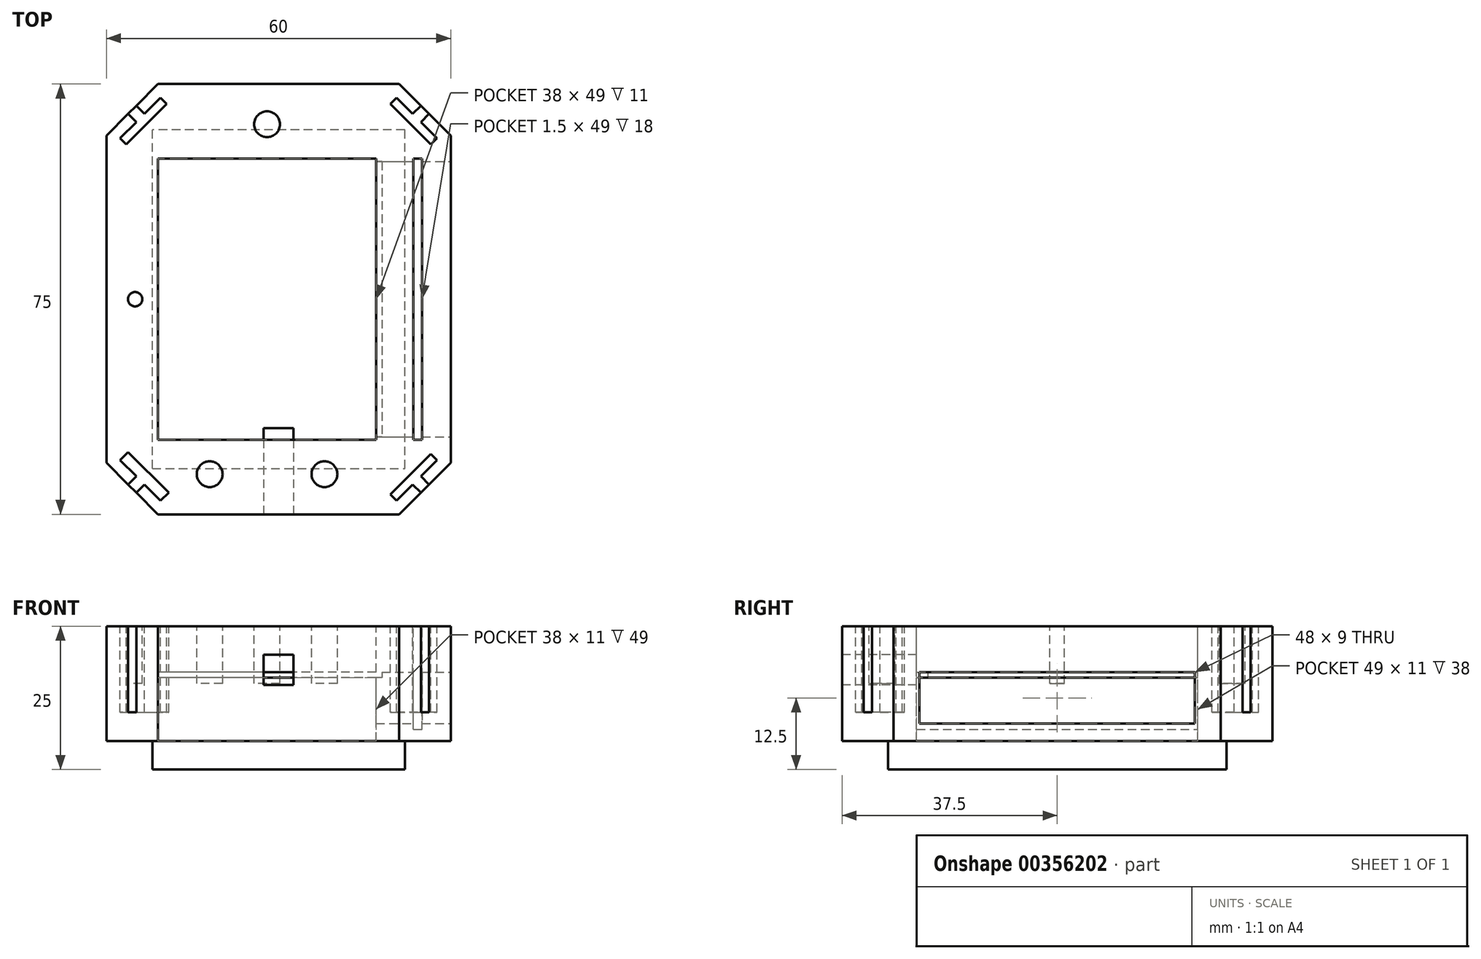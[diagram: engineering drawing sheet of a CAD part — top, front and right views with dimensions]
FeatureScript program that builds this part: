
annotation { "Feature Type Name" : "Feature", "Feature Type Description" : "" }
export const myFeature = defineFeature(function(context is Context, id is Id, definition is map)
    precondition{}
    {
        {
            var Q0;
            Q0=qCreatedBy(makeId("Top.planeOp"),FACE);
            var sketch = newSketch(context, id + "F0", { "sketchPlane" : qUnion([Q0])});
            skPoint(sketch, "E0", {"position": v(0, 66) * mm});
            skPoint(sketch, "E1", {"position": v(9, 75) * mm});
            skPoint(sketch, "E2", {"position": v(51, 75) * mm});
            skPoint(sketch, "E3", {"position": v(60, 66) * mm});
            skPoint(sketch, "E4", {"position": v(0, 9) * mm});
            skPoint(sketch, "E5", {"position": v(9, 0) * mm});
            skPoint(sketch, "E6", {"position": v(51, 0) * mm});
            skPoint(sketch, "E7", {"position": v(60, 9) * mm});
            skLineSegment(sketch, "E8", {"start": v(0, 9) * mm, "end": v(9, 0) * mm});
            skLineSegment(sketch, "E9", {"start": v(51, 0) * mm, "end": v(9, 0) * mm});
            skLineSegment(sketch, "E10", {"start": v(51, 0) * mm, "end": v(60, 9) * mm});
            skLineSegment(sketch, "E11", {"start": v(60, 9) * mm, "end": v(60, 66) * mm});
            skLineSegment(sketch, "E12", {"start": v(60, 66) * mm, "end": v(51, 75) * mm});
            skLineSegment(sketch, "E13", {"start": v(51, 75) * mm, "end": v(9, 75) * mm});
            skLineSegment(sketch, "E14", {"start": v(9, 75) * mm, "end": v(0, 66) * mm});
            skLineSegment(sketch, "E15", {"start": v(0, 66) * mm, "end": v(0, 9) * mm});
            skPoint(sketch, "E16", {"position": v(0, 63) * mm});
            skSolve(sketch);
        }
        {
            var Q0;
            Q0 = qSketchRegion(id + "F0", true);
            extrude(context, id + "F1", {"entities" : qUnion([Q0]), "depth" : 20 * mm, "offsetDistance" : 25 * mm});
        }
        {
            var Q0;
            Q0 = qSketchRegion(id + "F0", true);
            extrude(context, id + "F2", {"entities" : qUnion([Q0]), "operationType" : NewBodyOperationType.ADD, "depth" : 20 * mm, "offsetDistance" : 25 * mm});
        }
        {
            var Q0;
            Q0=makeQuery(id+"F1.opExtrude","CAP_FACE",FACE,{"disambiguationData":[OSD([sQuery(id+"F0.wireOp",EDGE,"E8"),sQuery(id+"F0.wireOp",EDGE,"E9"),sQuery(id+"F0.wireOp",EDGE,"E10"),sQuery(id+"F0.wireOp",EDGE,"E11"),sQuery(id+"F0.wireOp",EDGE,"E12"),sQuery(id+"F0.wireOp",EDGE,"E13"),sQuery(id+"F0.wireOp",EDGE,"E14"),sQuery(id+"F0.wireOp",EDGE,"E15")])],"isStart":false});
            var sketch = newSketch(context, id + "F3", { "sketchPlane" : qUnion([Q0])});
            skPoint(sketch, "E17", {"position": v(4.5, 70.5) * mm});
            skPoint(sketch, "E18", {"position": v(5.2, 71.2) * mm});
            skPoint(sketch, "E19", {"position": v(3.8, 69.8) * mm});
            skPoint(sketch, "E20", {"position": v(3.8, 5.2) * mm});
            skPoint(sketch, "E21", {"position": v(4.5, 4.5) * mm});
            skPoint(sketch, "E22", {"position": v(5.2, 3.8) * mm});
            skPoint(sketch, "E23", {"position": v(54.8, 3.8) * mm});
            skPoint(sketch, "E24", {"position": v(55.5, 4.5) * mm});
            skPoint(sketch, "E25", {"position": v(56.2, 5.2) * mm});
            skPoint(sketch, "E26", {"position": v(56.2, 69.8) * mm});
            skPoint(sketch, "E27", {"position": v(55.5, 70.5) * mm});
            skPoint(sketch, "E28", {"position": v(54.8, 71.2) * mm});
            skLineSegment(sketch, "E29", {"start": v(3.8, 69.8) * mm, "end": v(5.2, 71.2) * mm});
            skLineSegment(sketch, "E30", {"start": v(5.2, 71.2) * mm, "end": v(6.62, 69.8) * mm});
            skLineSegment(sketch, "E31", {"start": v(6.62, 69.8) * mm, "end": v(5.2, 68.38) * mm});
            skLineSegment(sketch, "E32", {"start": v(5.2, 68.38) * mm, "end": v(3.8, 69.8) * mm});
            skLineSegment(sketch, "E33", {"start": v(6.62, 69.8) * mm, "end": v(9.45, 72.62) * mm});
            skLineSegment(sketch, "E34", {"start": v(9.45, 72.62) * mm, "end": v(5.2, 68.38) * mm});
            skLineSegment(sketch, "E35", {"start": v(5.2, 68.38) * mm, "end": v(2.38, 65.55) * mm});
            skLineSegment(sketch, "E36", {"start": v(2.38, 65.55) * mm, "end": v(3.44, 64.49) * mm});
            skLineSegment(sketch, "E37", {"start": v(3.44, 64.49) * mm, "end": v(10.51, 71.56) * mm});
            skLineSegment(sketch, "E38", {"start": v(10.51, 71.56) * mm, "end": v(9.45, 72.62) * mm});
            skLineSegment(sketch, "E39", {"start": v(54.8, 71.2) * mm, "end": v(56.2, 69.8) * mm});
            skLineSegment(sketch, "E40", {"start": v(56.2, 69.8) * mm, "end": v(54.8, 68.38) * mm});
            skLineSegment(sketch, "E41", {"start": v(54.8, 68.38) * mm, "end": v(53.38, 69.8) * mm});
            skLineSegment(sketch, "E42", {"start": v(53.38, 69.8) * mm, "end": v(54.8, 71.2) * mm});
            skLineSegment(sketch, "E43", {"start": v(53.38, 69.8) * mm, "end": v(50.55, 72.62) * mm});
            skLineSegment(sketch, "E44", {"start": v(50.55, 72.62) * mm, "end": v(49.49, 71.56) * mm});
            skLineSegment(sketch, "E45", {"start": v(49.49, 71.56) * mm, "end": v(56.56, 64.49) * mm});
            skLineSegment(sketch, "E46", {"start": v(56.56, 64.49) * mm, "end": v(57.62, 65.55) * mm});
            skLineSegment(sketch, "E47", {"start": v(57.62, 65.55) * mm, "end": v(54.8, 68.38) * mm});
            skLineSegment(sketch, "E48", {"start": v(54.8, 3.8) * mm, "end": v(56.2, 5.2) * mm});
            skLineSegment(sketch, "E49", {"start": v(56.2, 5.2) * mm, "end": v(54.8, 6.62) * mm});
            skLineSegment(sketch, "E50", {"start": v(54.8, 6.62) * mm, "end": v(53.38, 5.2) * mm});
            skLineSegment(sketch, "E51", {"start": v(53.38, 5.2) * mm, "end": v(54.8, 3.8) * mm});
            skLineSegment(sketch, "E52", {"start": v(54.8, 6.62) * mm, "end": v(57.62, 9.45) * mm});
            skLineSegment(sketch, "E53", {"start": v(57.62, 9.45) * mm, "end": v(56.56, 10.51) * mm});
            skLineSegment(sketch, "E54", {"start": v(56.56, 10.51) * mm, "end": v(49.49, 3.44) * mm});
            skLineSegment(sketch, "E55", {"start": v(49.49, 3.44) * mm, "end": v(50.55, 2.38) * mm});
            skLineSegment(sketch, "E56", {"start": v(50.55, 2.38) * mm, "end": v(53.38, 5.2) * mm});
            skLineSegment(sketch, "E57", {"start": v(3.8, 5.2) * mm, "end": v(5.2, 3.8) * mm});
            skLineSegment(sketch, "E58", {"start": v(5.2, 3.8) * mm, "end": v(6.62, 5.2) * mm});
            skLineSegment(sketch, "E59", {"start": v(6.62, 5.2) * mm, "end": v(5.2, 6.62) * mm});
            skLineSegment(sketch, "E60", {"start": v(5.2, 6.62) * mm, "end": v(3.8, 5.2) * mm});
            skLineSegment(sketch, "E61", {"start": v(5.2, 6.62) * mm, "end": v(2.38, 9.45) * mm});
            skLineSegment(sketch, "E62", {"start": v(2.38, 9.45) * mm, "end": v(3.8, 10.86) * mm});
            skLineSegment(sketch, "E63", {"start": v(3.8, 10.86) * mm, "end": v(10.86, 3.8) * mm});
            skLineSegment(sketch, "E64", {"start": v(10.86, 3.8) * mm, "end": v(9.45, 2.38) * mm});
            skLineSegment(sketch, "E65", {"start": v(9.45, 2.38) * mm, "end": v(6.62, 5.2) * mm});
            skSolve(sketch);
        }
        {
            var Q0;
            Q0=makeQuery(id+"F3.imprint","IMPRINT",FACE,{"disambiguationData":[TD([[makeQuery(id+"F3.imprint","IMPRINT",EDGE,{"derivedFrom":sQuery(id+"F3.wireOp",EDGE,"E29")}),1.0]])]});
            var Q1;
            {var subQ0=sQuery(id+"F3.wireOp",EDGE,"E35");Q1=makeQuery(id+"F3.imprint","IMPRINT",FACE,{"disambiguationData":[TD([[makeQuery(id+"F3.imprint","IMPRINT",EDGE,{"derivedFrom":subQ0}),1.0]])]});}
            var Q2;
            Q2=makeQuery(id+"F3.imprint","IMPRINT",FACE,{"disambiguationData":[TD([[makeQuery(id+"F3.imprint","IMPRINT",EDGE,{"derivedFrom":sQuery(id+"F3.wireOp",EDGE,"E59")}),-1.0]])]});
            var Q3;
            Q3=makeQuery(id+"F3.imprint","IMPRINT",FACE,{"disambiguationData":[TD([[makeQuery(id+"F3.imprint","IMPRINT",EDGE,{"derivedFrom":sQuery(id+"F3.wireOp",EDGE,"E57")}),1.0]])]});
            var Q4;
            Q4=makeQuery(id+"F3.imprint","IMPRINT",FACE,{"disambiguationData":[TD([[makeQuery(id+"F3.imprint","IMPRINT",EDGE,{"derivedFrom":sQuery(id+"F3.wireOp",EDGE,"E48")}),1.0]])]});
            var Q5;
            Q5=makeQuery(id+"F3.imprint","IMPRINT",FACE,{"disambiguationData":[TD([[makeQuery(id+"F3.imprint","IMPRINT",EDGE,{"derivedFrom":sQuery(id+"F3.wireOp",EDGE,"E50")}),-1.0]])]});
            var Q6;
            Q6=makeQuery(id+"F3.imprint","IMPRINT",FACE,{"disambiguationData":[TD([[makeQuery(id+"F3.imprint","IMPRINT",EDGE,{"derivedFrom":sQuery(id+"F3.wireOp",EDGE,"E41")}),1.0]])]});
            var Q7;
            Q7=makeQuery(id+"F3.imprint","IMPRINT",FACE,{"disambiguationData":[TD([[makeQuery(id+"F3.imprint","IMPRINT",EDGE,{"derivedFrom":sQuery(id+"F3.wireOp",EDGE,"E39")}),1.0]])]});
            extrude(context, id + "F4", {"entities" : qUnion([Q0, Q1, Q2, Q3, Q4, Q5, Q6, Q7]), "operationType" : NewBodyOperationType.REMOVE, "oppositeDirection" : true, "depth" : 15 * mm, "offsetDistance" : 25 * mm});
        }
        {
            var Q0;
            Q0=makeQuery(id+"F1.opExtrude","CAP_FACE",FACE,{"disambiguationData":[OSD([sQuery(id+"F0.wireOp",EDGE,"E8"),sQuery(id+"F0.wireOp",EDGE,"E9"),sQuery(id+"F0.wireOp",EDGE,"E10"),sQuery(id+"F0.wireOp",EDGE,"E11"),sQuery(id+"F0.wireOp",EDGE,"E12"),sQuery(id+"F0.wireOp",EDGE,"E13"),sQuery(id+"F0.wireOp",EDGE,"E14"),sQuery(id+"F0.wireOp",EDGE,"E15")])],"isStart":false});
            var sketch = newSketch(context, id + "F5", { "sketchPlane" : qUnion([Q0])});
            skPoint(sketch, "E66", {"position": v(0, 62) * mm});
            skPoint(sketch, "E67", {"position": v(13, 75) * mm});
            skPoint(sketch, "E68", {"position": v(47, 75) * mm});
            skPoint(sketch, "E69", {"position": v(60, 62) * mm});
            skPoint(sketch, "E70", {"position": v(60, 13) * mm});
            skPoint(sketch, "E71", {"position": v(47, 0) * mm});
            skPoint(sketch, "E72", {"position": v(13, 0) * mm});
            skPoint(sketch, "E73", {"position": v(0, 13) * mm});
            skPoint(sketch, "E74", {"position": v(13, 62) * mm});
            skPoint(sketch, "E75", {"position": v(47, 62) * mm});
            skPoint(sketch, "E76", {"position": v(47, 13) * mm});
            skPoint(sketch, "E77", {"position": v(13, 13) * mm});
            skLineSegment(sketch, "E78", {"start": v(13, 62) * mm, "end": v(47, 62) * mm});
            skLineSegment(sketch, "E79", {"start": v(47, 13) * mm, "end": v(47, 62) * mm});
            skLineSegment(sketch, "E80", {"start": v(13, 62) * mm, "end": v(13, 13) * mm});
            skLineSegment(sketch, "E81", {"start": v(13, 13) * mm, "end": v(47, 13) * mm});
            skPoint(sketch, "E82", {"position": v(8, 8) * mm});
            skPoint(sketch, "E83", {"position": v(8, 67) * mm});
            skPoint(sketch, "E84", {"position": v(52, 67) * mm});
            skPoint(sketch, "E85", {"position": v(52, 8) * mm});
            skLineSegment(sketch, "E86", {"start": v(52, 8) * mm, "end": v(52, 67) * mm});
            skLineSegment(sketch, "E87", {"start": v(52, 67) * mm, "end": v(8, 67) * mm});
            skLineSegment(sketch, "E88", {"start": v(8, 8) * mm, "end": v(8, 67) * mm});
            skLineSegment(sketch, "E89", {"start": v(8, 8) * mm, "end": v(52, 8) * mm});
            skSolve(sketch);
        }
        {
            var Q0;
            Q0=makeQuery(id+"F1.opExtrude","SWEPT_FACE",FACE,{"disambiguationData":[OSD([sQuery(id+"F0.wireOp",EDGE,"E11")])]});
            var sketch = newSketch(context, id + "F6", { "sketchPlane" : qUnion([Q0])});
            skPoint(sketch, "E90", {"position": v(37.5, 20) * mm});
            skPoint(sketch, "E91", {"position": v(61.5, 20) * mm});
            skPoint(sketch, "E92", {"position": v(13.5, 20) * mm});
            skPoint(sketch, "E93", {"position": v(13.5, 12) * mm});
            skPoint(sketch, "E94", {"position": v(61.5, 3) * mm});
            skPoint(sketch, "E95", {"position": v(13.5, 3) * mm});
            skPoint(sketch, "E96", {"position": v(61.5, 12) * mm});
            skLineSegment(sketch, "E97", {"start": v(13.5, 12) * mm, "end": v(61.5, 12) * mm});
            skLineSegment(sketch, "E98", {"start": v(61.5, 3) * mm, "end": v(61.5, 12) * mm});
            skLineSegment(sketch, "E99", {"start": v(61.5, 3) * mm, "end": v(13.5, 3) * mm});
            skLineSegment(sketch, "E100", {"start": v(13.5, 3) * mm, "end": v(13.5, 12) * mm});
            skSolve(sketch);
        }
        {
            var Q0;
            Q0=makeQuery(id+"F5.imprint","IMPRINT",FACE,{"disambiguationData":[TD([[makeQuery(id+"F5.imprint","IMPRINT",EDGE,{"derivedFrom":sQuery(id+"F5.wireOp",EDGE,"E78")}),-1.0]])]});
            var Q1;
            Q1=makeQuery(id+"F5.imprint","IMPRINT",FACE,{"disambiguationData":[TD([[makeQuery(id+"F5.imprint","IMPRINT",EDGE,{"derivedFrom":sQuery(id+"F5.wireOp",EDGE,"E78")}),1.0]])]});
            extrude(context, id + "F7", {"entities" : qUnion([Q0, Q1]), "operationType" : NewBodyOperationType.ADD, "oppositeDirection" : true, "depth" : 25 * mm, "offsetDistance" : 25 * mm});
        }
        {
            var Q0;
            Q0=makeQuery(id+"F5.imprint","IMPRINT",FACE,{"disambiguationData":[TD([[makeQuery(id+"F5.imprint","IMPRINT",EDGE,{"derivedFrom":sQuery(id+"F5.wireOp",EDGE,"E78")}),-1.0]])]});
            extrude(context, id + "F8", {"entities" : qUnion([Q0]), "operationType" : NewBodyOperationType.REMOVE, "oppositeDirection" : true, "depth" : 20 * mm, "offsetDistance" : 25 * mm});
        }
        {
            var Q0;
            Q0 = qSketchRegion(id + "F6", true);
            extrude(context, id + "F9", {"entities" : qUnion([Q0]), "operationType" : NewBodyOperationType.REMOVE, "oppositeDirection" : true, "depth" : 45 * mm, "offsetDistance" : 25 * mm});
        }
        {
            var Q0;
            Q0=makeQuery(id+"F1.opExtrude","CAP_FACE",FACE,{"disambiguationData":[OSD([sQuery(id+"F0.wireOp",EDGE,"E8"),sQuery(id+"F0.wireOp",EDGE,"E9"),sQuery(id+"F0.wireOp",EDGE,"E10"),sQuery(id+"F0.wireOp",EDGE,"E11"),sQuery(id+"F0.wireOp",EDGE,"E12"),sQuery(id+"F0.wireOp",EDGE,"E13"),sQuery(id+"F0.wireOp",EDGE,"E14"),sQuery(id+"F0.wireOp",EDGE,"E15")])],"isStart":false});
            var sketch = newSketch(context, id + "F10", { "sketchPlane" : qUnion([Q0])});
            skPoint(sketch, "E101", {"position": v(55, 13) * mm});
            skPoint(sketch, "E102", {"position": v(55, 62) * mm});
            skLineSegment(sketch, "E103", {"start": v(55, 13) * mm, "end": v(55, 62) * mm});
            skLineSegment(sketch, "E104", {"start": v(55, 62) * mm, "end": v(53.5, 62) * mm});
            skLineSegment(sketch, "E105", {"start": v(53.5, 62) * mm, "end": v(53.5, 13) * mm});
            skLineSegment(sketch, "E106", {"start": v(53.5, 13) * mm, "end": v(55, 13) * mm});
            skSolve(sketch);
        }
        {
            var Q0;
            Q0 = qSketchRegion(id + "F10", true);
            extrude(context, id + "F11", {"entities" : qUnion([Q0]), "operationType" : NewBodyOperationType.REMOVE, "oppositeDirection" : true, "depth" : 18 * mm, "offsetDistance" : 25 * mm});
        }
        {
            var Q0;
            Q0=makeQuery(id+"F8.boolean.opBoolean","COPY",FACE,{"derivedFrom":makeQuery(id+"F8.opExtrude","SWEPT_FACE",FACE,{"disambiguationData":[OSD([sQuery(id+"F5.wireOp",EDGE,"E80")])]})});
            var sketch = newSketch(context, id + "F12", { "sketchPlane" : qUnion([Q0])});
            skLineSegment(sketch, "E107.bottom", {"start": v(13, 20) * mm, "end": v(62, 20) * mm});
            skLineSegment(sketch, "E107.top", {"start": v(13, 0) * mm, "end": v(62, 0) * mm});
            skLineSegment(sketch, "E107.left", {"start": v(13, 20) * mm, "end": v(13, 0) * mm});
            skLineSegment(sketch, "E107.right", {"start": v(62, 20) * mm, "end": v(62, 0) * mm});
            skSolve(sketch);
        }
        {
            var Q0;
            Q0 = qSketchRegion(id + "F12", true);
            extrude(context, id + "F13", {"entities" : qUnion([Q0]), "operationType" : NewBodyOperationType.REMOVE, "oppositeDirection" : true, "depth" : 4 * mm, "offsetDistance" : 25 * mm});
        }
        {
            var Q0;
            Q0=makeQuery(id+"F13.boolean.opBoolean","COPY",FACE,{"derivedFrom":makeQuery(id+"F13.opExtrude","CAP_FACE",FACE,{"disambiguationData":[OSD([sQuery(id+"F12.wireOp",EDGE,"E107.bottom"),sQuery(id+"F12.wireOp",EDGE,"E107.top"),sQuery(id+"F12.wireOp",EDGE,"E107.left"),sQuery(id+"F12.wireOp",EDGE,"E107.right")])],"isStart":false})});
            var sketch = newSketch(context, id + "F14", { "sketchPlane" : qUnion([Q0])});
            skPoint(sketch, "E108", {"position": v(13, 12) * mm});
            skPoint(sketch, "E109", {"position": v(62, 12) * mm});
            skLineSegment(sketch, "E110", {"start": v(13, 12) * mm, "end": v(62, 12) * mm});
            skLineSegment(sketch, "E111", {"start": v(62, 12) * mm, "end": v(62, 11) * mm});
            skLineSegment(sketch, "E112", {"start": v(62, 11) * mm, "end": v(13, 11) * mm});
            skLineSegment(sketch, "E113", {"start": v(13, 11) * mm, "end": v(13, 12) * mm});
            skSolve(sketch);
        }
        {
            var Q0;
            Q0 = qSketchRegion(id + "F14", true);
            extrude(context, id + "F15", {"entities" : qUnion([Q0]), "operationType" : NewBodyOperationType.ADD, "depth" : 39 * mm, "offsetDistance" : 25 * mm});
        }
        {
            var Q0;
            Q0=makeQuery(id+"F1.opExtrude","CAP_FACE",FACE,{"disambiguationData":[OSD([sQuery(id+"F0.wireOp",EDGE,"E8"),sQuery(id+"F0.wireOp",EDGE,"E9"),sQuery(id+"F0.wireOp",EDGE,"E10"),sQuery(id+"F0.wireOp",EDGE,"E11"),sQuery(id+"F0.wireOp",EDGE,"E12"),sQuery(id+"F0.wireOp",EDGE,"E13"),sQuery(id+"F0.wireOp",EDGE,"E14"),sQuery(id+"F0.wireOp",EDGE,"E15")])],"isStart":false});
            var sketch = newSketch(context, id + "F16", { "sketchPlane" : qUnion([Q0])});
            skPoint(sketch, "E114", {"position": v(28, 62) * mm});
            skPoint(sketch, "E115", {"position": v(9, 37.5) * mm});
            skPoint(sketch, "E116", {"position": v(47, 37.5) * mm});
            skPoint(sketch, "E117", {"position": v(18, 7) * mm});
            skPoint(sketch, "E118", {"position": v(5, 37.5) * mm});
            skPoint(sketch, "E119", {"position": v(28, 68) * mm});
            skCircle(sketch, "E120", {"center": v(18, 7) * mm, "radius": 2.25 * mm});
            skCircle(sketch, "E121", {"center": v(28, 68) * mm, "radius": 2.25 * mm});
            skCircle(sketch, "E122", {"center": v(5, 37.5) * mm, "radius": 1.25 * mm});
            skPoint(sketch, "E123", {"position": v(28, 13) * mm});
            skPoint(sketch, "E124", {"position": v(18, 13) * mm});
            skPoint(sketch, "E125", {"position": v(38, 13) * mm});
            skPoint(sketch, "E126", {"position": v(38, 7) * mm});
            skCircle(sketch, "E127", {"center": v(38, 7) * mm, "radius": 2.25 * mm});
            skSolve(sketch);
        }
        {
            var Q0;
            Q0 = qSketchRegion(id + "F16", true);
            extrude(context, id + "F17", {"entities" : qUnion([Q0]), "operationType" : NewBodyOperationType.REMOVE, "oppositeDirection" : true, "depth" : 10 * mm, "offsetDistance" : 25 * mm});
        }
        {
            var Q0;
            Q0=makeQuery(id+"F1.opExtrude","SWEPT_FACE",FACE,{"disambiguationData":[OSD([sQuery(id+"F0.wireOp",EDGE,"E9")])]});
            var sketch = newSketch(context, id + "F18", { "sketchPlane" : qUnion([Q0])});
            skPoint(sketch, "E128", {"position": v(30, 20) * mm});
            skPoint(sketch, "E129", {"position": v(32.62, 20) * mm});
            skPoint(sketch, "E130", {"position": v(27.38, 20) * mm});
            skPoint(sketch, "E131", {"position": v(27.38, 15) * mm});
            skPoint(sketch, "E132", {"position": v(32.62, 15) * mm});
            skLineSegment(sketch, "E133", {"start": v(27.38, 15) * mm, "end": v(32.62, 15) * mm});
            skLineSegment(sketch, "E134", {"start": v(32.62, 15) * mm, "end": v(32.62, 9.75) * mm});
            skLineSegment(sketch, "E135", {"start": v(32.62, 9.75) * mm, "end": v(27.38, 9.75) * mm});
            skLineSegment(sketch, "E136", {"start": v(27.38, 9.75) * mm, "end": v(27.38, 15) * mm});
            skSolve(sketch);
        }
        {
            var Q0;
            Q0 = qSketchRegion(id + "F18", true);
            extrude(context, id + "F19", {"entities" : qUnion([Q0]), "operationType" : NewBodyOperationType.REMOVE, "oppositeDirection" : true, "depth" : 15 * mm, "offsetDistance" : 25 * mm});
        }
    });
